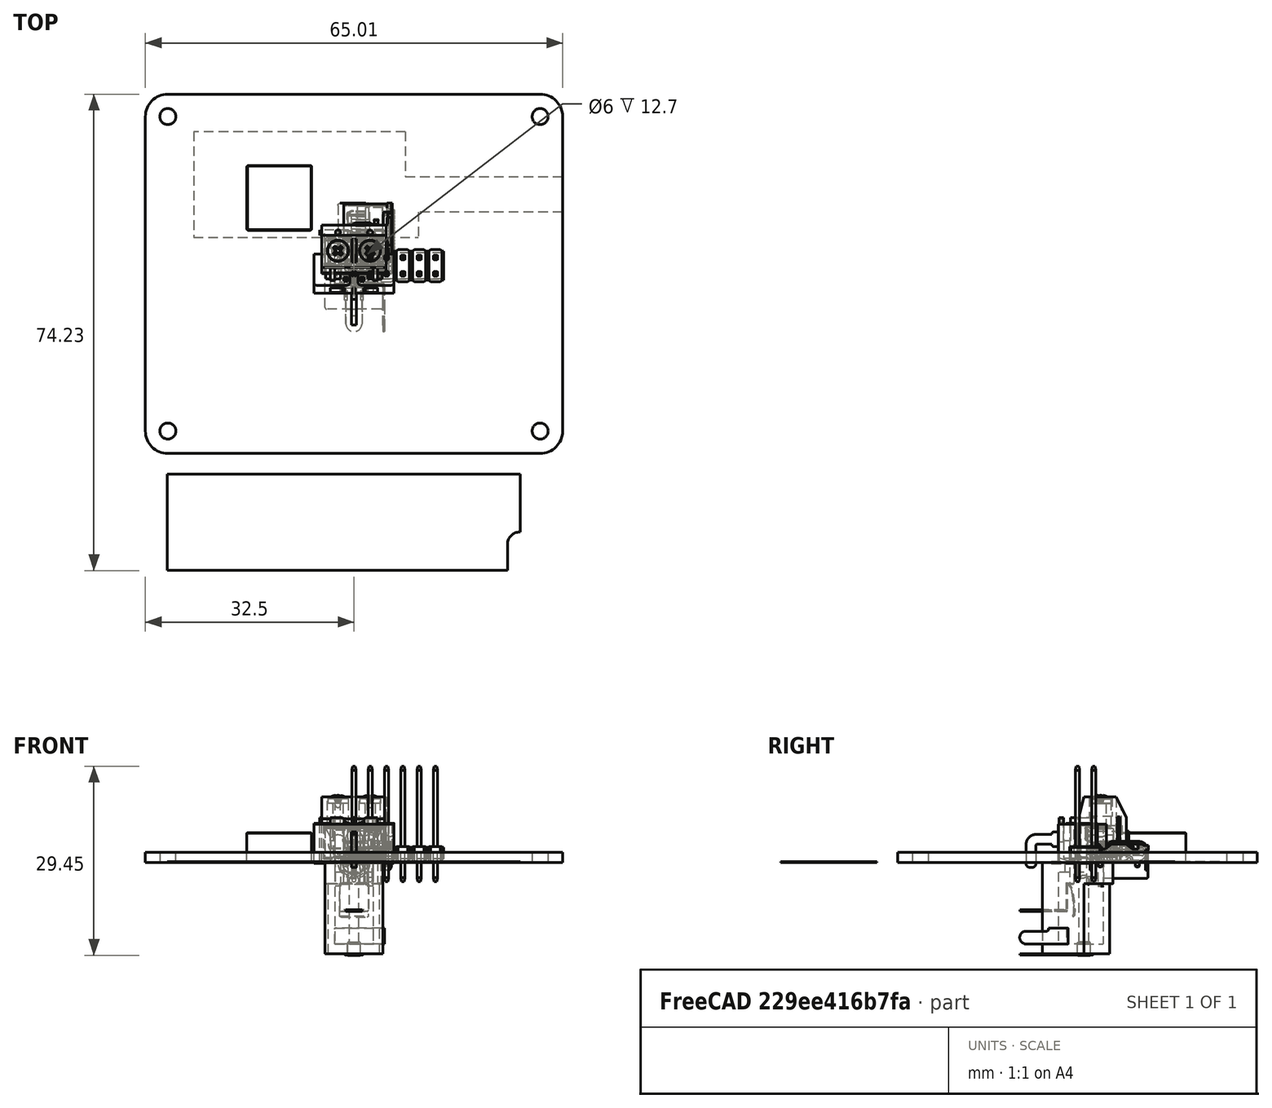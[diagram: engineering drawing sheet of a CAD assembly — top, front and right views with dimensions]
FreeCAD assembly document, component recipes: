
FREECAD ASSEMBLY — COMPONENT RECIPES ("Yahboom PDB")

This assembly document has 16 components, labeled P0..P15 below (a component is one placed body or linked part). 5 of them carry a construction recipe — the FreeCAD feature program that regenerates the part from scratch, quoted from this document or its linked companion documents; the rest are supplied as boundary geometry only. No exploded tour is included for this assembly.
COMPONENT P0 — geometry summary ("B2B-PH-K-S v007"; no construction recipe available for this part):
  bounding box: 9.4 x 5.9 x 4.5 mm
  tessellated surface: 484 triangles
  volume: 77 mm^3 (31% of its bounding box)
  symmetry: mirror-symmetric across its x mid-plane
COMPONENT P1 — geometry summary ("B2B-PH-K-S v008"; no construction recipe available for this part):
  bounding box: 9.4 x 5.9 x 4.5 mm
  tessellated surface: 484 triangles
  volume: 77 mm^3 (31% of its bounding box)
  symmetry: mirror-symmetric across its x mid-plane
COMPONENT P2 — recipe-attached ("Board001", modeled in this document).
Construction recipe (the document's own serialized feature program — sketch geometry with constraints, then the solid features built on it; lengths are millimeters unless a unit is written):

FEATURE [Sketcher::SketchObject] Sketch001
  ArcFitTolerance = 1e-06
  AttachmentSupport = -> [XY_Plane001]
  FullyConstrained = true
  MakeInternals = false
  MapMode = 5
  sketch-geometry (23):
    g0: LineSegment StartX=-32.5 StartY=24.5 StartZ=0 EndX=-32.5 EndY=-24.5 EndZ=0
    g1: LineSegment StartX=-29 StartY=-28 StartZ=0 EndX=29 EndY=-28 EndZ=0
    g2: LineSegment StartX=32.5 StartY=-24.5 StartZ=0 EndX=32.5 EndY=24.5 EndZ=0
    g3: LineSegment StartX=29 StartY=28 StartZ=0 EndX=-29 EndY=28 EndZ=0
    g4: Circle CenterX=-29 CenterY=-24.5 CenterZ=0 NormalX=0 NormalY=0 NormalZ=1 AngleXU=0 Radius=1.25
    g5: GeomPoint X=-32.5 Y=0 Z=0
    g6: GeomPoint X=0 Y=28 Z=0
    g7: Circle CenterX=29 CenterY=-24.5 CenterZ=0 NormalX=0 NormalY=0 NormalZ=1 AngleXU=0 Radius=1.25
    g8: LineSegment [constr] StartX=-29 StartY=-24.5 StartZ=0 EndX=29 EndY=-24.5 EndZ=0
    g9: LineSegment [constr] StartX=-29 StartY=-24.5 StartZ=0 EndX=-29 EndY=24.5 EndZ=0
    g10: LineSegment [constr] StartX=-29 StartY=24.5 StartZ=0 EndX=29 EndY=24.5 EndZ=0
    g11: Circle CenterX=-29 CenterY=24.5 CenterZ=0 NormalX=0 NormalY=0 NormalZ=1 AngleXU=0 Radius=1.25
    g12: Circle CenterX=29 CenterY=24.5 CenterZ=0 NormalX=0 NormalY=0 NormalZ=1 AngleXU=0 Radius=1.25
    g13: GeomPoint [constr] X=-29 Y=0 Z=0
    g14: ArcOfCircle CenterX=-29 CenterY=24.5 CenterZ=0 NormalX=0 NormalY=0 NormalZ=1 AngleXU=0 Radius=3.5 StartAngle=1.5708 EndAngle=3.14159
    g15: GeomPoint [constr] X=-32.5 Y=28 Z=0
    g16: ArcOfCircle CenterX=29 CenterY=24.5 CenterZ=0 NormalX=0 NormalY=0 NormalZ=1 AngleXU=0 Radius=3.5 StartAngle=0 EndAngle=1.5708
    g17: GeomPoint [constr] X=32.5 Y=28 Z=0
    g18: ArcOfCircle CenterX=-29 CenterY=-24.5 CenterZ=0 NormalX=0 NormalY=0 NormalZ=1 AngleXU=0 Radius=3.5 StartAngle=3.14159 EndAngle=4.71239
    g19: GeomPoint [constr] X=-32.5 Y=-28 Z=0
    g20: ArcOfCircle CenterX=29 CenterY=-24.5 CenterZ=0 NormalX=0 NormalY=0 NormalZ=1 AngleXU=0 Radius=3.5 StartAngle=4.71239 EndAngle=6.28319
    g21: GeomPoint [constr] X=32.5 Y=-28 Z=0
    g22: GeomPoint X=0 Y=24.5 Z=0
  constraints (50):
    c: Vertical(g0)
    c: Vertical(g2)
    c: Horizontal(g1)
    c: Horizontal(g3)
    c: DistanceX(g15,g17) = 65
    c: DistanceY(g19,g15) = 56
    c: Diameter(g4) = 2.5
    c: Symmetric(g15,g19,g5)
    c: Horizontal(g5,g-1)
    c: Symmetric(g17,g15,g6)
    c: Vertical(g6,g-1)
    c: Diameter(g7) = 2.5
    c: Horizontal(g4,g7)
    c: Coincident(g8,g4)
    c: Coincident(g8,g7)
    c: Vertical(g9)
    c: Coincident(g10,g9)
    c: Horizontal(g10)
    c: Coincident(g11,g9)
    c: Coincident(g12,g10)
    c: Diameter(g11) = 2.5
    c: Diameter(g12) = 2.5
    c: DistanceX(g8,g8) = 58
    c: DistanceY(g9,g9) = 49
    c: DistanceX(g10,g10) = 58
    c: Coincident(g9,g4)
    c: Symmetric(g9,g9,g13)
    c: Horizontal(g13,g-1)
    c: PointOnObject(g15,g0)
    c: PointOnObject(g15,g3)
    c: Tangent(g0,g14) = -1.5708
    c: Tangent(g3,g14) = -1.5708
    c: PointOnObject(g17,g2)
    c: PointOnObject(g17,g3)
    c: Tangent(g2,g16) = -1.5708
    c: Tangent(g3,g16) = -1.5708
    c: PointOnObject(g19,g0)
    c: PointOnObject(g19,g1)
    c: Tangent(g0,g18) = -1.5708
    c: Tangent(g1,g18) = -1.5708
    c: PointOnObject(g21,g1)
    c: PointOnObject(g21,g2)
    c: Tangent(g1,g20) = -1.5708
    c: Tangent(g2,g20) = -1.5708
    c: Radius(g14) = 3.5
    c: Radius(g16) = 3.5
    c: Radius(g20) = 3.5
    c: Radius(g18) = 3.5
    c: Symmetric(g10,g10,g22)
    c: Vertical(g22,g-1)
FEATURE [PartDesign::Pad] Pad
  Direction = (0,0,1)
  Length = 1.57
  Length2 = 10
  Profile = -> Sketch001
  ReferenceAxis = -> Sketch001 [N_Axis]
  Refine = true
  Suppressed = false
  Type = 0
FEATURE [PartDesign::Body] Body  label="Board"
  AllowCompound = false
  Group = -> [Sketch001,Pad]
  Origin = -> Origin001
  Tip = -> Pad
COMPONENT P3 — recipe-attached ("Board_Decal003", modeled in this document).
Construction recipe (the document's own serialized feature program — sketch geometry with constraints, then the solid features built on it; lengths are millimeters unless a unit is written):

FEATURE [Sketcher::SketchObject] Sketch009
  ArcFitTolerance = 1e-06
  AttachmentSupport = -> [XY_Plane019]
  FullyConstrained = false
  MakeInternals = false
  MapMode = 5
  sketch-geometry (8):
    g0: LineSegment StartX=8.01058 StartY=22.151 StartZ=0 EndX=-24.9894 EndY=22.151 EndZ=0
    g1: LineSegment StartX=-24.9894 StartY=22.151 StartZ=0 EndX=-24.9894 EndY=5.65103 EndZ=0
    g2: LineSegment StartX=-24.9894 StartY=5.65103 StartZ=0 EndX=10.0106 EndY=5.65103 EndZ=0
    g3: LineSegment StartX=8.01058 StartY=22.151 StartZ=0 EndX=8.01058 EndY=15.151 EndZ=0
    g4: LineSegment StartX=8.01058 StartY=15.151 StartZ=0 EndX=32.5106 EndY=15.151 EndZ=0
    g5: LineSegment StartX=32.5106 StartY=15.151 StartZ=0 EndX=32.5106 EndY=9.65103 EndZ=0
    g6: LineSegment StartX=32.5106 StartY=9.65103 StartZ=0 EndX=10.0106 EndY=9.65103 EndZ=0
    g7: LineSegment StartX=10.0106 StartY=9.65103 StartZ=0 EndX=10.0106 EndY=5.65103 EndZ=0
  constraints (22):
    c: Horizontal(g0)
    c: Coincident(g1,g0)
    c: Vertical(g1)
    c: Coincident(g2,g1)
    c: Horizontal(g2)
    c: Coincident(g3,g0)
    c: Vertical(g3)
    c: Coincident(g4,g3)
    c: Horizontal(g4)
    c: Coincident(g5,g4)
    c: Vertical(g5)
    c: Coincident(g6,g5)
    c: Horizontal(g6)
    c: Coincident(g7,g6)
    c: Coincident(g7,g2)
    c: Vertical(g7)
    c: DistanceY(g1,g1) = 16.5
    c: DistanceX(g0,g0) = 33
    c: DistanceX(g2,g2) = 35
    c: DistanceY(g5,g5) = 5.5
    c: DistanceY(g3,g3) = 7
    c: DistanceX(g6,g6) = 22.5
FEATURE [PartDesign::Pad] Pad005
  Direction = (0,0,1)
  Length = 0.1
  Length2 = 10
  Profile = -> Sketch009
  ReferenceAxis = -> Sketch009 [N_Axis]
  Refine = true
  Suppressed = false
  Type = 0
FEATURE [PartDesign::Body] Body005  label="Board_Decal001"
  AllowCompound = false
  Group = -> [Sketch009,Pad005]
  Origin = -> Origin019
  Tip = -> Pad005
COMPONENT P4 — recipe-attached ("Board_Decal004", modeled in this document).
Construction recipe (the document's own serialized feature program — sketch geometry with constraints, then the solid features built on it; lengths are millimeters unless a unit is written):

FEATURE [Sketcher::SketchObject] Sketch010
  ArcFitTolerance = 1e-06
  AttachmentSupport = -> [XY_Plane020]
  FullyConstrained = false
  MakeInternals = false
  MapMode = 5
  sketch-geometry (8):
    g0: LineSegment StartX=-29.0787 StartY=-31.2258 StartZ=0 EndX=25.9213 EndY=-31.2258 EndZ=0
    g1: LineSegment StartX=25.9213 StartY=-31.2258 StartZ=0 EndX=25.9213 EndY=-40.2258 EndZ=0
    g2: LineSegment StartX=25.9213 StartY=-40.2258 StartZ=0 EndX=25.8213 EndY=-40.2258 EndZ=0
    g3: LineSegment StartX=23.9213 StartY=-42.1258 StartZ=0 EndX=23.9213 EndY=-46.2258 EndZ=0
    g4: LineSegment StartX=23.9213 StartY=-46.2258 StartZ=0 EndX=-29.0787 EndY=-46.2258 EndZ=0
    g5: LineSegment StartX=-29.0787 StartY=-46.2258 StartZ=0 EndX=-29.0787 EndY=-31.2258 EndZ=0
    g6: ArcOfCircle CenterX=25.8213 CenterY=-42.1258 CenterZ=0 NormalX=0 NormalY=0 NormalZ=1 AngleXU=0 Radius=1.9 StartAngle=1.5708 EndAngle=3.14159
    g7: GeomPoint [constr] X=23.9213 Y=-40.2258 Z=0
  constraints (20):
    c: Horizontal(g0)
    c: Coincident(g1,g0)
    c: Vertical(g1)
    c: Coincident(g2,g1)
    c: Horizontal(g2)
    c: Vertical(g3)
    c: Coincident(g4,g3)
    c: Horizontal(g4)
    c: Coincident(g5,g4)
    c: Coincident(g5,g0)
    c: Vertical(g5)
    c: DistanceY(g5,g5) = 15
    c: DistanceX(g0,g0) = 55
    c: DistanceX(g4,g4) = 53
    c: DistanceY(g1,g1) = 9
    c: PointOnObject(g7,g2)
    c: PointOnObject(g7,g3)
    c: Tangent(g2,g6) = -1.5708
    c: Tangent(g3,g6) = -1.5708
    c: Radius(g6) = 1.9
FEATURE [PartDesign::Pad] Pad006
  Direction = (0,0,1)
  Length = 0.1
  Length2 = 10
  Profile = -> Sketch010
  ReferenceAxis = -> Sketch010 [N_Axis]
  Refine = true
  Suppressed = false
  Type = 0
FEATURE [PartDesign::Body] Body006  label="Board_Decal002"
  AllowCompound = false
  Group = -> [Sketch010,Pad006]
  Origin = -> Origin020
  Tip = -> Pad006
COMPONENT P5 — geometry summary ("DC_JACK v007"; no construction recipe available for this part):
  bounding box: 14.5 x 14.4 x 9.3 mm
  tessellated surface: 20,236 triangles
  volume: 812 mm^3 (42% of its bounding box)
COMPONENT P6 — geometry summary ("DC_JACK v008"; no construction recipe available for this part):
  bounding box: 14.5 x 14.4 x 9.3 mm
  tessellated surface: 20,236 triangles
  volume: 812 mm^3 (42% of its bounding box)
COMPONENT P7 — geometry summary ("DS1021_black_2x06p_100mil_Type5_rev1.019"; no construction recipe available for this part):
  bounding box: 18.0 x 15.2 x 5.0 mm
  tessellated surface: 2,864 triangles
  volume: 231 mm^3 (17% of its bounding box)
  symmetry: 2-fold rotationally symmetric about the y axis; mirror-symmetric across its x mid-plane, z mid-plane
COMPONENT P8 — recipe-attached ("Switch001", modeled in this document).
Construction recipe (the document's own serialized feature program — sketch geometry with constraints, then the solid features built on it; lengths are millimeters unless a unit is written):

FEATURE [Sketcher::SketchObject] Sketch
  ArcFitTolerance = 1e-06
  FullyConstrained = true
  MakeInternals = false
  MapMode = 5
  sketch-geometry (6):
    g0: LineSegment StartX=6.25 StartY=-3 StartZ=0 EndX=6.25 EndY=3 EndZ=0
    g1: LineSegment StartX=6.25 StartY=3 StartZ=0 EndX=-6.25 EndY=3 EndZ=0
    g2: LineSegment StartX=-6.25 StartY=3 StartZ=0 EndX=-6.25 EndY=-3 EndZ=0
    g3: LineSegment StartX=-6.25 StartY=-3 StartZ=0 EndX=6.25 EndY=-3 EndZ=0
    g4: GeomPoint X=-6.25 Y=0 Z=0
    g5: GeomPoint X=0 Y=3 Z=0
  constraints (14):
    c: Coincident(g0,g1)
    c: Coincident(g1,g2)
    c: Coincident(g2,g3)
    c: Coincident(g3,g0)
    c: Vertical(g0)
    c: Vertical(g2)
    c: Horizontal(g1)
    c: Horizontal(g3)
    c: DistanceX(g1,g1) = 12.5
    c: DistanceY(g2,g2) = 6
    c: Symmetric(g2,g2,g4)
    c: Symmetric(g1,g1,g5)
    c: Vertical(g5,g-1)
    c: Horizontal(g4,g-1)
FEATURE [PartDesign::Pad] Pad001
  Direction = (0,0,1)
  Length = 6
  Length2 = 10
  Profile = -> Sketch
  ReferenceAxis = -> Sketch [N_Axis]
  Refine = true
  Suppressed = false
  Type = 0
FEATURE [Sketcher::SketchObject] Sketch003
  ArcFitTolerance = 1e-06
  AttachmentSupport = -> [Extrude]
  ExternalGeometry = -> [Extrude]
  FullyConstrained = true
  MakeInternals = false
  MapMode = 5
  Placement = pos=(0,0,6.1) rot=(0,0,1;0rad)
  sketch-geometry (14):
    g0: LineSegment StartX=-0.625 StartY=-1.8 StartZ=0 EndX=0.625 EndY=-1.8 EndZ=0
    g1: LineSegment StartX=0.625 StartY=-1.8 StartZ=0 EndX=0.625 EndY=0.7 EndZ=0
    g2: LineSegment StartX=0.625 StartY=0.7 StartZ=0 EndX=-0.625 EndY=0.7 EndZ=0
    g3: LineSegment StartX=-0.625 StartY=0.7 StartZ=0 EndX=-0.625 EndY=-1.8 EndZ=0
    g4: GeomPoint X=-2e-16 Y=-1.8 Z=0
    g5: GeomPoint X=-2e-16 Y=-1.8 Z=0
    g6: LineSegment StartX=2.125 StartY=0.7 StartZ=0 EndX=2.125 EndY=-0.8 EndZ=0
    g7: LineSegment StartX=2.125 StartY=-0.8 StartZ=0 EndX=4.375 EndY=-0.8 EndZ=0
    g8: LineSegment StartX=4.375 StartY=-0.8 StartZ=0 EndX=4.375 EndY=0.7 EndZ=0
    g9: LineSegment StartX=4.375 StartY=0.7 StartZ=0 EndX=2.125 EndY=0.7 EndZ=0
    g10: LineSegment StartX=-2.125 StartY=0.7 StartZ=0 EndX=-4.375 EndY=0.7 EndZ=0
    g11: LineSegment StartX=-4.375 StartY=0.7 StartZ=0 EndX=-4.375 EndY=-0.8 EndZ=0
    g12: LineSegment StartX=-4.375 StartY=-0.8 StartZ=0 EndX=-2.125 EndY=-0.8 EndZ=0
    g13: LineSegment StartX=-2.125 StartY=-0.8 StartZ=0 EndX=-2.125 EndY=0.7 EndZ=0
  constraints (38):
    c: Coincident(g0,g1)
    c: Coincident(g1,g2)
    c: Coincident(g2,g3)
    c: Coincident(g3,g0)
    c: Horizontal(g0)
    c: Horizontal(g2)
    c: Vertical(g1)
    c: Vertical(g3)
    c: Symmetric(g-3,g-3,g4)
    c: Symmetric(g0,g0,g5)
    c: Vertical(g4,g5)
    c: DistanceX(g2,g2) = 1.25
    c: DistanceY(g1,g1) = 2.5
    c: Coincident(g6,g7)
    c: Coincident(g7,g8)
    c: Coincident(g8,g9)
    c: Coincident(g9,g6)
    c: Vertical(g6)
    c: Vertical(g8)
    c: Horizontal(g7)
    c: Horizontal(g9)
    c: DistanceX(g9,g9) = 2.25
    c: DistanceY(g6,g6) = 1.5
    c: Distance(g1,g6) = 1.5
    c: Horizontal(g1,g6)
    c: Distance(g-3,g7) = 1
    c: Coincident(g10,g11)
    c: Coincident(g11,g12)
    c: Coincident(g12,g13)
    c: Coincident(g13,g10)
    c: Horizontal(g10)
    c: Horizontal(g12)
    c: Vertical(g11)
    c: Vertical(g13)
    c: Horizontal(g10,g2)
    c: DistanceX(g10,g10) = 2.25
    c: DistanceY(g13,g13) = 1.5
    c: Distance(g3,g13) = 1.5
FEATURE [PartDesign::FeatureBase] BaseFeature
  BaseFeature = -> Extrude
  Suppressed = false
FEATURE [PartDesign::Pocket] Pocket
  BaseFeature = -> BaseFeature
  Direction = (0,0,-1)
  Length = 5
  Length2 = 5
  Profile = -> Sketch003
  ReferenceAxis = -> Sketch003 [N_Axis]
  Refine = true
  Suppressed = false
  Type = 0
FEATURE [PartDesign::Fillet] Fillet
  Base = -> Pocket [Edge32,Edge35,Edge39,Edge37,Edge31,Edge23,Edge19,Edge27]
  BaseFeature = -> Pocket
  Radius = 0.5
  Refine = true
  SupportTransform = false
  Suppressed = false
  UseAllEdges = false
FEATURE [Sketcher::SketchObject] Sketch005
  ArcFitTolerance = 1e-06
  AttachmentSupport = -> [Fillet]
  FullyConstrained = true
  MakeInternals = false
  MapMode = 5
  Placement = pos=(0,3,0) rot=(1,0,0;1.5708rad)
  sketch-geometry (5):
    g0: LineSegment StartX=-3.25 StartY=5 StartZ=0 EndX=-3.25 EndY=1 EndZ=0
    g1: LineSegment StartX=-3.25 StartY=1 StartZ=0 EndX=3.25 EndY=1 EndZ=0
    g2: LineSegment StartX=3.25 StartY=1 StartZ=0 EndX=3.25 EndY=5 EndZ=0
    g3: LineSegment StartX=3.25 StartY=5 StartZ=0 EndX=-3.25 EndY=5 EndZ=0
    g4: GeomPoint X=0 Y=1 Z=0
  constraints (13):
    c: Coincident(g0,g1)
    c: Coincident(g1,g2)
    c: Coincident(g2,g3)
    c: Coincident(g3,g0)
    c: Vertical(g0)
    c: Vertical(g2)
    c: Horizontal(g1)
    c: Horizontal(g3)
    c: DistanceY(g2,g2) = 4
    c: DistanceX(g3,g3) = 6.5
    c: Symmetric(g1,g1,g4)
    c: Vertical(g-1,g4)
    c: Distance(g1,g-1) = 1
FEATURE [PartDesign::Pocket] Pocket001
  BaseFeature = -> Fillet
  Direction = (0,1,-2e-16)
  Length = 5
  Length2 = 5
  Profile = -> Sketch005
  ReferenceAxis = -> Sketch005 [N_Axis]
  Refine = true
  Suppressed = false
  Type = 0
FEATURE [PartDesign::Body] Body001  label="Casing"
  AllowCompound = false
  BaseFeature = -> Extrude
  Group = -> [BaseFeature,Sketch003,Pocket,Fillet,Sketch005,Pocket001]
  Origin = -> Origin015
  Tip = -> Pocket001
FEATURE [Sketcher::SketchObject] Sketch006
  ArcFitTolerance = 1e-06
  AttachmentSupport = -> [XZ_Plane016]
  FullyConstrained = true
  MakeInternals = false
  MapMode = 5
  Placement = pos=(0,0,0) rot=(1,0,0;1.5708rad)
  sketch-geometry (4):
    g0: LineSegment StartX=3.25 StartY=4.9 StartZ=0 EndX=-0.55 EndY=4.9 EndZ=0
    g1: LineSegment StartX=-0.55 StartY=4.9 StartZ=0 EndX=-0.55 EndY=1.1 EndZ=0
    g2: LineSegment StartX=-0.55 StartY=1.1 StartZ=0 EndX=3.25 EndY=1.1 EndZ=0
    g3: LineSegment StartX=3.25 StartY=1.1 StartZ=0 EndX=3.25 EndY=4.9 EndZ=0
  constraints (12):
    c: Coincident(g0,g1)
    c: Coincident(g1,g2)
    c: Coincident(g2,g3)
    c: Coincident(g3,g0)
    c: Horizontal(g0)
    c: Horizontal(g2)
    c: Vertical(g1)
    c: Vertical(g3)
    c: DistanceX(g0,g0) = 3.8
    c: DistanceY(g1,g1) = 3.8
    c: Distance(g-1,g2) = 1.1
    c: Distance(g-2,g3) = 3.25
FEATURE [PartDesign::Pad] Pad002
  BaseFeature = -> Pad001
  Direction = (0,-1,2e-16)
  Length = 8
  Length2 = 10
  Profile = -> Sketch006
  ReferenceAxis = -> Sketch006 [N_Axis]
  Refine = true
  Reversed = true
  Suppressed = false
  Type = 0
FEATURE [PartDesign::Chamfer] Chamfer
  Angle = 60
  Base = -> Pad002 [Edge24,Edge21]
  BaseFeature = -> Pad002
  ChamferType = 2
  FlipDirection = false
  Refine = true
  Size = 0.5
  Size2 = 1
  SupportTransform = false
  Suppressed = false
  UseAllEdges = false
FEATURE [PartDesign::Body] Body002  label="Body + Knob"
  AllowCompound = false
  Group = -> [Pad001,Sketch,Sketch006,Pad002,Chamfer]
  Origin = -> Origin016
  Tip = -> Chamfer
FEATURE [Sketcher::SketchObject] Sketch007
  ArcFitTolerance = 1e-06
  AttachmentSupport = -> [YZ_Plane017]
  FullyConstrained = true
  MakeInternals = false
  MapMode = 5
  Placement = pos=(0,0,0) rot=(0.57735,0.57735,0.57735;2.0944rad)
  sketch-geometry (10):
    g0: LineSegment StartX=-3 StartY=4.75 StartZ=0 EndX=-4 EndY=4.75 EndZ=0
    g1: LineSegment StartX=-4 StartY=2.5 StartZ=0 EndX=-3 EndY=2.5 EndZ=0
    g2: LineSegment StartX=-3 StartY=4.75 StartZ=0 EndX=-3 EndY=2.5 EndZ=0
    g3: LineSegment StartX=-4 StartY=4.375 StartZ=0 EndX=-8 EndY=4.375 EndZ=0
    g4: LineSegment StartX=-8 StartY=4.375 StartZ=0 EndX=-8 EndY=-0.75 EndZ=0
    g5: LineSegment StartX=-4 StartY=2.875 StartZ=0 EndX=-6.5 EndY=2.875 EndZ=0
    g6: LineSegment StartX=-6.5 StartY=2.875 StartZ=0 EndX=-6.5 EndY=-0.75 EndZ=0
    g7: LineSegment StartX=-4 StartY=4.75 StartZ=0 EndX=-4 EndY=4.375 EndZ=0
    g8: LineSegment StartX=-4 StartY=2.875 StartZ=0 EndX=-4 EndY=2.5 EndZ=0
    g9: LineSegment StartX=-8 StartY=-0.75 StartZ=0 EndX=-6.5 EndY=-0.75 EndZ=0
  constraints (30):
    c: Horizontal(g0)
    c: Horizontal(g1)
    c: DistanceX(g0,g0) = 1
    c: Distance(g1,g0) = 2.25
    c: Coincident(g2,g0)
    c: Vertical(g2)
    c: Coincident(g1,g2)
    c: Distance(g-2,g2) = 3
    c: Horizontal(g3)
    c: Coincident(g4,g3)
    c: Vertical(g4)
    c: Horizontal(g5)
    c: Coincident(g6,g5)
    c: Vertical(g6)
    c: Distance(g5,g3) = 1.5
    c: Distance(g6,g4) = 1.5
    c: Distance(g-1,g5) = 2.875
    c: Distance(g-1,g1) = 2.5
    c: DistanceX(g3,g3) = 4
    c: Coincident(g7,g3)
    c: Vertical(g7)
    c: Coincident(g8,g5)
    c: Coincident(g8,g1)
    c: Vertical(g8)
    c: Coincident(g0,g7)
    c: Vertical(g5,g3)
    c: Coincident(g9,g4)
    c: Coincident(g9,g6)
    c: Horizontal(g9)
    c: DistanceY(g6,g6) = 3.625
FEATURE [PartDesign::Pad] Pad003
  Direction = (1,0,0)
  Length = 0.75
  Length2 = 10
  Midplane = true
  Placement = pos=(0,0,0) rot=(1,1,1;2.0944rad)
  Profile = -> Sketch007
  ReferenceAxis = -> Sketch007 [N_Axis]
  Refine = true
  Suppressed = false
  Type = 0
FEATURE [PartDesign::Fillet] Fillet001
  Base = -> Pad003 [Edge17]
  BaseFeature = -> Pad003
  Placement = pos=(0,0,0) rot=(1,1,1;2.0944rad)
  Radius = 1.5
  Refine = true
  SupportTransform = false
  Suppressed = false
  UseAllEdges = false
FEATURE [PartDesign::Fillet] Fillet002
  Base = -> Fillet001 [Edge17,Edge32,Edge31]
  BaseFeature = -> Fillet001
  Placement = pos=(0,0,0) rot=(1,1,1;2.0944rad)
  Radius = 0.25
  Refine = true
  SupportTransform = false
  Suppressed = false
  UseAllEdges = false
FEATURE [PartDesign::Fillet] Fillet003
  Base = -> Fillet002 [Edge28,Edge32]
  BaseFeature = -> Fillet002
  Placement = pos=(0,0,0) rot=(1,1,1;2.0944rad)
  Radius = 0.5
  Refine = true
  SupportTransform = false
  Suppressed = false
  UseAllEdges = false
FEATURE [PartDesign::Body] Body003  label="Connection001"
  AllowCompound = false
  Group = -> [Sketch007,Pad003,Fillet001,Fillet002,Fillet003]
  Origin = -> Origin017
  Tip = -> Fillet003
COMPONENT P9 — geometry summary ("USB Type C005"; no construction recipe available for this part):
  bounding box: 9.2 x 8.0 x 4.5 mm
  tessellated surface: 10,160 triangles
  volume: 113 mm^3 (35% of its bounding box)
COMPONENT P10 — geometry summary ("XH 2,54_2p004"; no construction recipe available for this part):
  bounding box: 10.4 x 7.4 x 5.8 mm
  tessellated surface: 380 triangles
  volume: 118 mm^3 (27% of its bounding box)
  symmetry: mirror-symmetric across its x mid-plane
COMPONENT P11 — recipe-attached ("4R008", modeled in this document).
Construction recipe (the document's own serialized feature program — sketch geometry with constraints, then the solid features built on it; lengths are millimeters unless a unit is written):

FEATURE [Sketcher::SketchObject] Sketch008
  ArcFitTolerance = 1e-06
  AttachmentSupport = -> [XY_Plane018]
  FullyConstrained = false
  MakeInternals = false
  MapMode = 5
  sketch-geometry (4):
    g0: LineSegment StartX=-16.6992 StartY=16.8811 StartZ=0 EndX=-16.6992 EndY=6.78113 EndZ=0
    g1: LineSegment StartX=-16.6992 StartY=6.78113 StartZ=0 EndX=-6.59923 EndY=6.78113 EndZ=0
    g2: LineSegment StartX=-6.59923 StartY=6.78113 StartZ=0 EndX=-6.59923 EndY=16.8811 EndZ=0
    g3: LineSegment StartX=-6.59923 StartY=16.8811 StartZ=0 EndX=-16.6992 EndY=16.8811 EndZ=0
  constraints (10):
    c: Coincident(g0,g1)
    c: Coincident(g1,g2)
    c: Coincident(g2,g3)
    c: Coincident(g3,g0)
    c: Vertical(g0)
    c: Vertical(g2)
    c: Horizontal(g1)
    c: Horizontal(g3)
    c: DistanceY(g2,g2) = 10.1
    c: DistanceX(g1,g1) = 10.1
FEATURE [PartDesign::Pad] Pad004
  Direction = (0,0,1)
  Length = 4.65
  Length2 = 10
  Profile = -> Sketch008
  ReferenceAxis = -> Sketch008 [N_Axis]
  Refine = true
  Suppressed = false
  Type = 0
FEATURE [PartDesign::Chamfer] Chamfer001
  Angle = 45
  Base = -> Pad004 [Face6,Face5]
  BaseFeature = -> Pad004
  ChamferType = 0
  FlipDirection = false
  Refine = true
  Size = 0.1
  Size2 = 1
  SupportTransform = false
  Suppressed = false
  UseAllEdges = false
FEATURE [PartDesign::Fillet] Fillet004
  Base = -> Chamfer001 [Edge4,Edge16,Edge5,Edge1]
  BaseFeature = -> Chamfer001
  Radius = 0.25
  Refine = true
  SupportTransform = false
  Suppressed = false
  UseAllEdges = false
FEATURE [PartDesign::Body] Body004  label="4R7"
  AllowCompound = false
  Group = -> [Sketch008,Pad004,Chamfer001,Fillet004]
  Origin = -> Origin018
  Tip = -> Fillet004
COMPONENT P12 — geometry summary ("4.7uF 63V electr 5 x11mm -P.diameter 2.5mm-Green-Yellow001"; no construction recipe available for this part):
  bounding box: 15.1 x 5.0 x 5.0 mm
  tessellated surface: 29,314 triangles
  volume: 210 mm^3 (56% of its bounding box)
  symmetry: 2-fold rotationally symmetric about the y axis; mirror-symmetric across its x mid-plane, z mid-plane
COMPONENT P13 — geometry summary ("4.7uF 63V electr 5 x11mm -P.diameter 2.5mm-Green-Yellow002"; no construction recipe available for this part):
  bounding box: 15.1 x 5.0 x 5.0 mm
  tessellated surface: 29,314 triangles
  volume: 210 mm^3 (56% of its bounding box)
  symmetry: 2-fold rotationally symmetric about the y axis; mirror-symmetric across its x mid-plane, z mid-plane
COMPONENT P14 — geometry summary ("4.7uF 63V electr 5 x11mm -P.diameter 2.5mm-Green-Yellow003"; no construction recipe available for this part):
  bounding box: 15.1 x 5.0 x 5.0 mm
  tessellated surface: 29,314 triangles
  volume: 210 mm^3 (56% of its bounding box)
  symmetry: 2-fold rotationally symmetric about the y axis; mirror-symmetric across its x mid-plane, z mid-plane
COMPONENT P15 — geometry summary ("kf301_v002"; no construction recipe available for this part):
  bounding box: 14.2 x 10.4 x 7.6 mm
  tessellated surface: 17,360 triangles
  volume: 476 mm^3 (43% of its bounding box)
PROVENANCE & LICENSES
A FreeCAD (.FCStd) document from a public repository crawl; recipes are the document's own serialized feature recipes (and, for linked parts, companion documents' recipes).
License: as declared in the source repository (recorded in the dataset sidecar).
